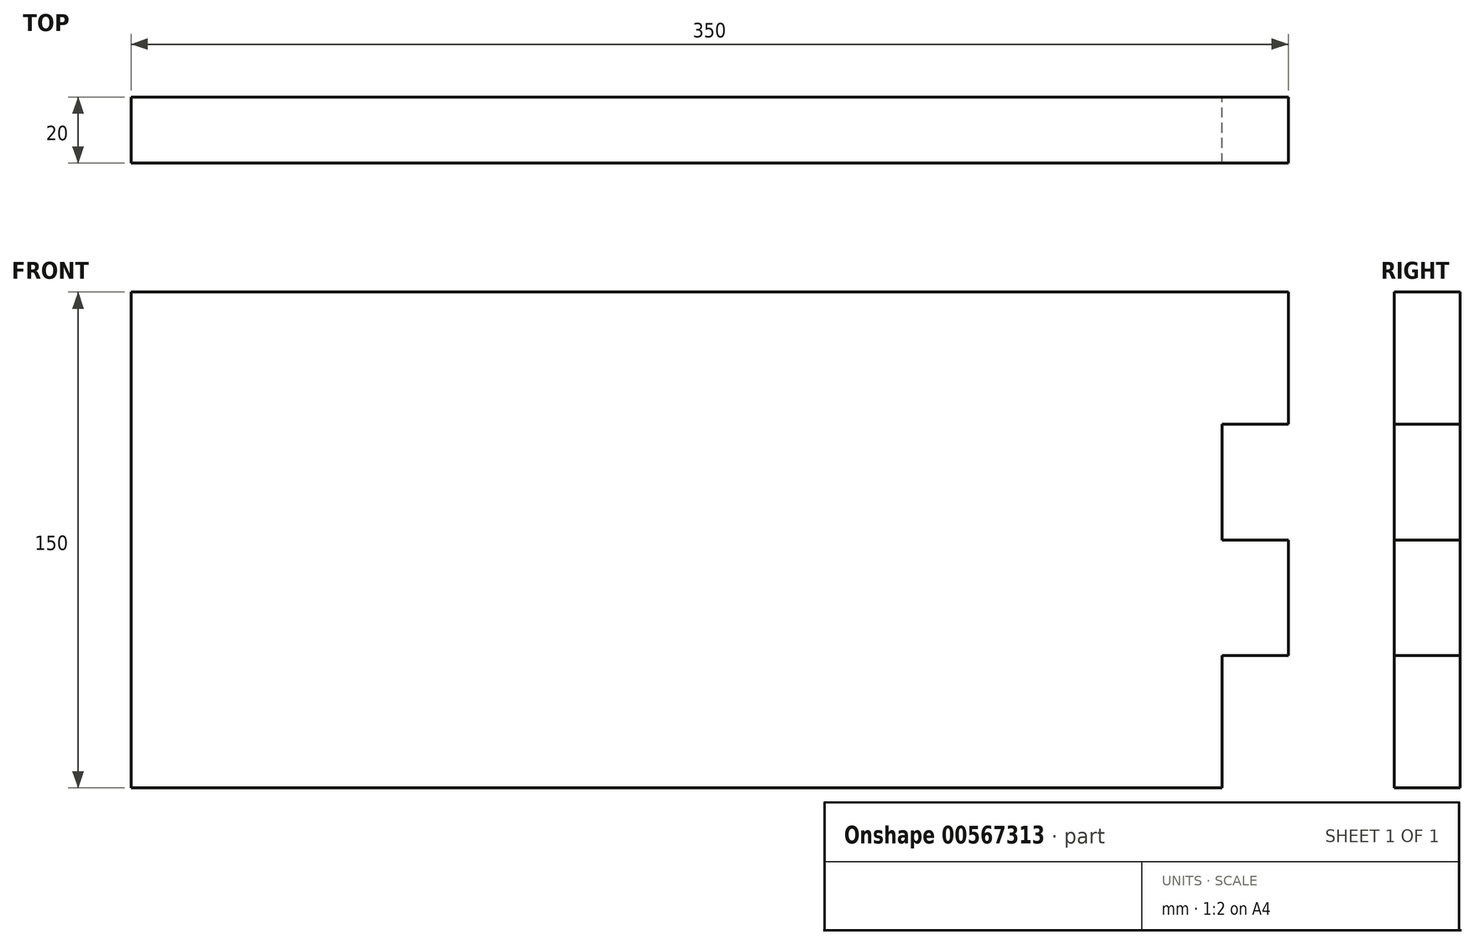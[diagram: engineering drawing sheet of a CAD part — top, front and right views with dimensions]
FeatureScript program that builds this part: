
annotation { "Feature Type Name" : "Feature", "Feature Type Description" : "" }
export const myFeature = defineFeature(function(context is Context, id is Id, definition is map)
    precondition{}
    {
        {
            var Q0;
            Q0=qCreatedBy(makeId("Front.planeOp"),FACE);
            var sketch = newSketch(context, id + "F0", { "sketchPlane" : qUnion([Q0])});
            skLineSegment(sketch, "E0.bottom", {"start": v(-211.01, 78.68) * mm, "end": v(138.99, 78.68) * mm});
            skLineSegment(sketch, "E0.top", {"start": v(-211.01, -71.32) * mm, "end": v(118.99, -71.32) * mm});
            skLineSegment(sketch, "E0.left", {"start": v(-211.01, 78.68) * mm, "end": v(-211.01, -71.32) * mm});
            skLineSegment(sketch, "E0.right", {"start": v(138.99, 78.68) * mm, "end": v(138.99, 38.68) * mm});
            skLineSegment(sketch, "E1", {"start": v(118.99, 78.68) * mm, "end": v(118.99, -71.32) * mm});
            skLineSegment(sketch, "E2", {"start": v(138.99, 3.68) * mm, "end": v(118.99, 3.68) * mm});
            skLineSegment(sketch, "E3", {"start": v(118.99, -31.32) * mm, "end": v(138.99, -31.32) * mm});
            skLineSegment(sketch, "E4", {"start": v(118.99, 38.68) * mm, "end": v(138.99, 38.68) * mm});
            skLineSegment(sketch, "E5.trimOffspring", {"start": v(138.99, 3.68) * mm, "end": v(138.99, -31.32) * mm});
            skPoint(sketch, "E6.orphan", {"position": v(138.99, -71.32) * mm});
            skSolve(sketch);
        }
        {
            var Q0;
            Q0 = qSketchRegion(id + "F0", true);
            extrude(context, id + "F1", {"entities" : qUnion([Q0]), "depth" : 20 * mm, "offsetDistance" : 25.4 * mm});
        }
    });
